# Revit family: Midea_VRF_MS01_E
name_source: partatom
category: Mechanical Equipment
revit_build: Autodesk Revit 2013 (Build: 20120221_2030(x64)
units: mm (PartAtom-declared; Revit-internal decimal feet)

## types (1)
- MS01/N1-D
    Casing color = SB2014
    Cooling Power Input = 57 W
    Depth = 295.000 mm
    Gas = R410A
    Gas pipes to IDU = ∅12.7/∅15.9
    Heating Power Input = 57 W
    Height = 196.000 mm
    High pressure gas pipe to ODU = ∅12.7/∅15.9/∅19.05
    Installation = Indoor installation
    Liquid pipe  to ODU = ∅9.52/∅12.7
    Liquid pipes to IDU = ∅6.35/∅9.52
    Low pressure gas pipe to ODU = ∅15.9/∅19.05/∅22.2
    Machine material = Galvanized Steel
    Manufacturer = Midea
    Max. No. of connectable indoor units = 8
    Max. No. of connectable indoor units per branch = 8
    Max. capacity index of connectable indoor units = 3.000 kW
    Max. capacity index of connectable indoor units per branch = 32.000 kW
    Maximum Fuse Amps = 15 A
    Minimum Circuit Amps = 0 A
    Model = MS01/N1-D
    Net Weight = 10.50 kg
    Number of branches = 1
    Power supply = 220-240V 1N~50Hz/60Hz
    Series = MS box
    Width = 440.000 mm

## geometry (parser evidence)
native form markers: Sweep x7
no freeform markers — native parametric forms only
